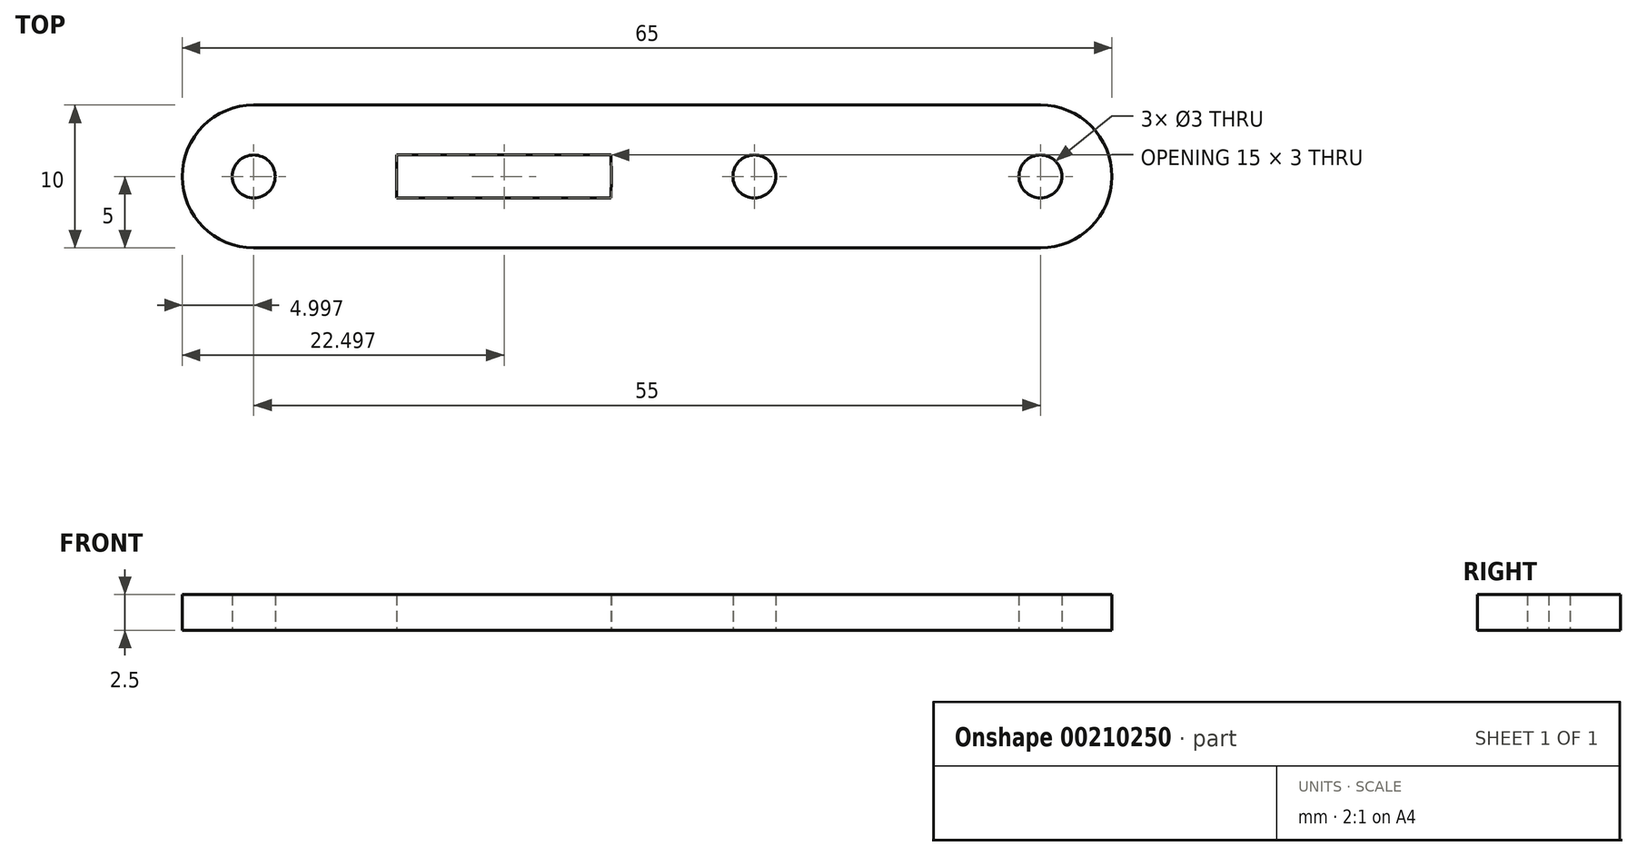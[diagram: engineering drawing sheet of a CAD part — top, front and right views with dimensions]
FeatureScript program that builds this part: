
annotation { "Feature Type Name" : "Feature", "Feature Type Description" : "" }
export const myFeature = defineFeature(function(context is Context, id is Id, definition is map)
    precondition{}
    {
        {
            var Q0;
            Q0=qCreatedBy(makeId("Top.planeOp"),FACE);
            var sketch = newSketch(context, id + "F0", { "sketchPlane" : qUnion([Q0])});
            skCircle(sketch, "E0", {"center": v(38.16, 0) * mm, "radius": 1.5 * mm});
            skArc(sketch, "E1", {"start": v(38.16, -5) * mm, "mid": v(43.16, 0) * mm, "end": v(38.16, 5) * mm});
            skLineSegment(sketch, "E2", {"start": v(38.16, 0) * mm, "end": v(36.66, 0) * mm});
            skLineSegment(sketch, "E3", {"start": v(-21.84, 0) * mm, "end": v(-21.84, 0) * mm});
            skLineSegment(sketch, "E4", {"start": v(-16.84, 5) * mm, "end": v(38.16, 5) * mm});
            skLineSegment(sketch, "E5.MirrorCS", {"start": v(-16.84, -5) * mm, "end": v(38.16, -5) * mm});
            skPoint(sketch, "E6", {"position": v(8.16, 0) * mm});
            skPoint(sketch, "E7", {"position": v(-6.84, 0) * mm});
            skPoint(sketch, "E8", {"position": v(-16.84, 0) * mm});
            skCircle(sketch, "E9", {"center": v(18.16, 0) * mm, "radius": 1.5 * mm});
            skCircle(sketch, "E10", {"center": v(-16.84, 0) * mm, "radius": 1.5 * mm});
            skLineSegment(sketch, "E11", {"start": v(-6.84, 0) * mm, "end": v(-6.84, 1.5) * mm});
            skLineSegment(sketch, "E12", {"start": v(-6.84, 1.5) * mm, "end": v(8.13, 1.5) * mm});
            skLineSegment(sketch, "E13", {"start": v(8.16, 0) * mm, "end": v(8.13, 1.5) * mm});
            skLineSegment(sketch, "E14.MirrorCS", {"start": v(8.16, 0) * mm, "end": v(8.13, -1.5) * mm});
            skLineSegment(sketch, "E15.MirrorCS", {"start": v(-6.84, -1.5) * mm, "end": v(8.13, -1.5) * mm});
            skLineSegment(sketch, "E16.MirrorCS", {"start": v(-6.84, 0) * mm, "end": v(-6.84, -1.5) * mm});
            skPoint(sketch, "E17.visualSharp", {"position": v(-21.84, 5) * mm});
            skArc(sketch, "E17.filletArc", {"start": v(-16.84, 5) * mm, "mid": v(-20.38, 3.54) * mm, "end": v(-21.84, 0) * mm});
            skPoint(sketch, "E18.visualSharp", {"position": v(-21.84, -5) * mm});
            skArc(sketch, "E18.filletArc", {"start": v(-21.84, 0) * mm, "mid": v(-20.38, -3.54) * mm, "end": v(-16.84, -5) * mm});
            skSolve(sketch);
        }
        {
            var Q0;
            Q0=makeQuery(id+"F0.imprint","IMPRINT",FACE,{"disambiguationData":[TD([[makeQuery(id+"F0.imprint","IMPRINT",EDGE,{"derivedFrom":sQuery(id+"F0.wireOp",EDGE,"E0")}),-1.0]])]});
            extrude(context, id + "F1", {"entities" : qUnion([Q0]), "depth" : 2.5 * mm});
        }
    });
